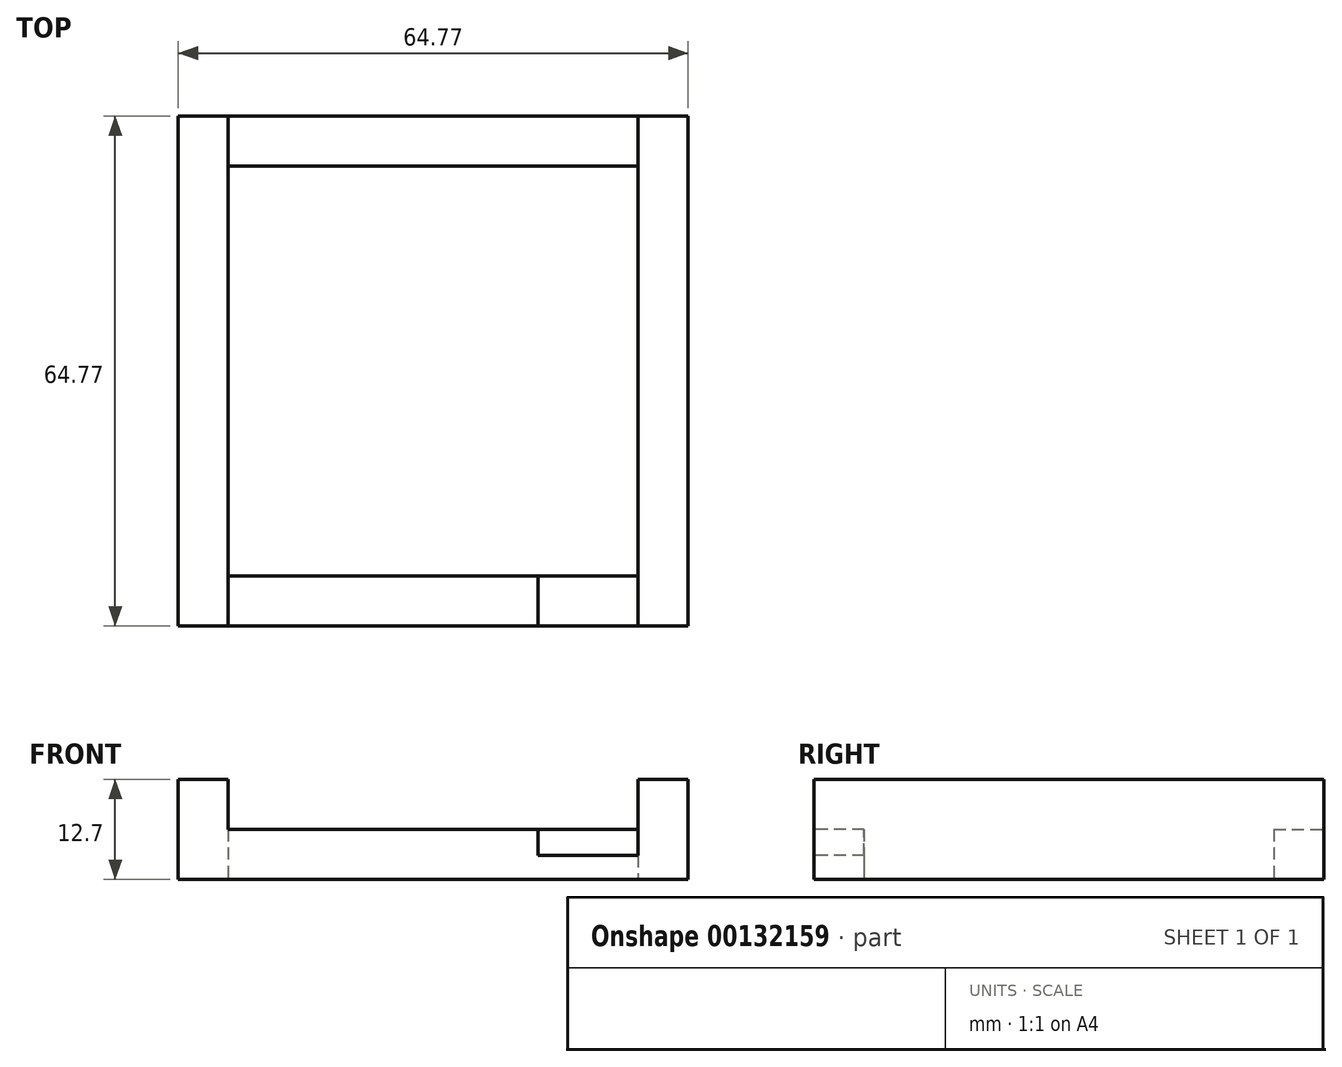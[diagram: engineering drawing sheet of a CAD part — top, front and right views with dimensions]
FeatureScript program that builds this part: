
annotation { "Feature Type Name" : "Feature", "Feature Type Description" : "" }
export const myFeature = defineFeature(function(context is Context, id is Id, definition is map)
    precondition{}
    {
        {
            var Q0;
            Q0=qCreatedBy(makeId("Top.planeOp"),FACE);
            var sketch = newSketch(context, id + "F0", { "sketchPlane" : qUnion([Q0])});
            skLineSegment(sketch, "E0.bottom", {"start": v(-17.09, 30.99) * mm, "end": v(34.98, 30.99) * mm});
            skLineSegment(sketch, "E0.top", {"start": v(-17.09, -21.08) * mm, "end": v(34.98, -21.08) * mm});
            skLineSegment(sketch, "E0.left", {"start": v(-17.09, 30.99) * mm, "end": v(-17.09, -21.08) * mm});
            skLineSegment(sketch, "E0.right", {"start": v(34.98, 30.99) * mm, "end": v(34.98, -21.08) * mm});
            skLineSegment(sketch, "E1", {"start": v(-17.09, 30.99) * mm, "end": v(-17.09, 37.34) * mm});
            skLineSegment(sketch, "E2", {"start": v(-17.09, 37.34) * mm, "end": v(-23.44, 37.34) * mm});
            skLineSegment(sketch, "E3.bottom", {"start": v(-23.44, 37.34) * mm, "end": v(41.33, 37.34) * mm});
            skLineSegment(sketch, "E3.top", {"start": v(-23.44, -27.43) * mm, "end": v(41.33, -27.43) * mm});
            skLineSegment(sketch, "E3.left", {"start": v(-23.44, 37.34) * mm, "end": v(-23.44, -27.43) * mm});
            skLineSegment(sketch, "E3.right", {"start": v(41.33, 37.34) * mm, "end": v(41.33, -27.43) * mm});
            skSolve(sketch);
        }
        {
            var Q0;
            Q0=makeQuery(id+"F0.imprint","IMPRINT",FACE,{"disambiguationData":[TD([[makeQuery(id+"F0.imprint","IMPRINT",EDGE,{"derivedFrom":sQuery(id+"F0.wireOp",EDGE,"E0.bottom")}),1.0]])]});
            extrude(context, id + "F1", {"entities" : qUnion([Q0]), "depth" : 12.7 * mm});
        }
        {
            var Q0;
            Q0=makeQuery(id+"F1.opExtrude","CAP_FACE",FACE,{"disambiguationData":[OSD([sQuery(id+"F0.wireOp",EDGE,"E0.bottom"),sQuery(id+"F0.wireOp",EDGE,"E0.top"),sQuery(id+"F0.wireOp",EDGE,"E0.left"),sQuery(id+"F0.wireOp",EDGE,"E0.right"),sQuery(id+"F0.wireOp",EDGE,"E3.bottom"),sQuery(id+"F0.wireOp",EDGE,"E3.top"),sQuery(id+"F0.wireOp",EDGE,"E3.left"),sQuery(id+"F0.wireOp",EDGE,"E3.right")])],"isStart":false});
            var sketch = newSketch(context, id + "F2", { "sketchPlane" : qUnion([Q0])});
            skLineSegment(sketch, "E4.bottom", {"start": v(34.98, -21.08) * mm, "end": v(-17.09, -21.08) * mm});
            skLineSegment(sketch, "E4.top", {"start": v(34.98, -27.43) * mm, "end": v(-17.09, -27.43) * mm});
            skLineSegment(sketch, "E4.left", {"start": v(34.98, -21.08) * mm, "end": v(34.98, -27.43) * mm});
            skLineSegment(sketch, "E4.right", {"start": v(-17.09, -21.08) * mm, "end": v(-17.09, -27.43) * mm});
            skLineSegment(sketch, "E5.bottom", {"start": v(-17.09, 30.99) * mm, "end": v(34.98, 30.99) * mm});
            skLineSegment(sketch, "E5.top", {"start": v(-17.09, 37.34) * mm, "end": v(34.98, 37.34) * mm});
            skLineSegment(sketch, "E5.left", {"start": v(-17.09, 30.99) * mm, "end": v(-17.09, 37.34) * mm});
            skLineSegment(sketch, "E5.right", {"start": v(34.98, 30.99) * mm, "end": v(34.98, 37.34) * mm});
            skSolve(sketch);
        }
        {
            var Q0;
            Q0=makeQuery(id+"F2.imprint","IMPRINT",FACE,{"disambiguationData":[TD([[makeQuery(id+"F2.imprint","IMPRINT",EDGE,{"derivedFrom":sQuery(id+"F2.wireOp",EDGE,"E5.bottom")}),1.0]])]});
            var Q1;
            Q1=makeQuery(id+"F2.imprint","IMPRINT",FACE,{"disambiguationData":[TD([[makeQuery(id+"F2.imprint","IMPRINT",EDGE,{"derivedFrom":sQuery(id+"F2.wireOp",EDGE,"E4.bottom")}),-1.0]])]});
            extrude(context, id + "F3", {"entities" : qUnion([Q0, Q1]), "operationType" : NewBodyOperationType.REMOVE, "oppositeDirection" : true, "depth" : 6.35 * mm});
        }
        {
            var Q0;
            Q0=makeQuery(id+"F3.boolean.opBoolean","COPY",FACE,{"derivedFrom":makeQuery(id+"F3.opExtrude","CAP_FACE",FACE,{"disambiguationData":[OSD([sQuery(id+"F2.wireOp",EDGE,"E4.bottom"),sQuery(id+"F2.wireOp",EDGE,"E4.top"),sQuery(id+"F2.wireOp",EDGE,"E4.left"),sQuery(id+"F2.wireOp",EDGE,"E4.right")])],"isStart":false})});
            var sketch = newSketch(context, id + "F4", { "sketchPlane" : qUnion([Q0])});
            skLineSegment(sketch, "E6.bottom", {"start": v(34.98, -21.08) * mm, "end": v(22.28, -21.08) * mm});
            skLineSegment(sketch, "E6.top", {"start": v(34.98, -27.43) * mm, "end": v(22.28, -27.43) * mm});
            skLineSegment(sketch, "E6.left", {"start": v(34.98, -21.08) * mm, "end": v(34.98, -27.43) * mm});
            skLineSegment(sketch, "E6.right", {"start": v(22.28, -21.08) * mm, "end": v(22.28, -27.43) * mm});
            skSolve(sketch);
        }
        {
            var Q0;
            Q0=makeQuery(id+"F4.imprint","IMPRINT",FACE,{"disambiguationData":[TD([[makeQuery(id+"F4.imprint","IMPRINT",EDGE,{"derivedFrom":sQuery(id+"F4.wireOp",EDGE,"E6.bottom")}),-1.0]])]});
            extrude(context, id + "F5", {"entities" : qUnion([Q0]), "operationType" : NewBodyOperationType.REMOVE, "oppositeDirection" : true, "depth" : 3.3 * mm});
        }
    });
